# Revit family: QF_EVEREST_ESC59L
name_source: partatom
category: Specialty Equipment
revit_build: Autodesk Revit 2015 (Build: 20140606_1530(x64)
units: mm (PartAtom-declared; Revit-internal decimal feet)

## types (1)
- ESC59L
    Apparent Power = 173 VA
    Conn Conduit = Yes
    Conn Plug = NEMA 5-15P
    Cycle = 60 Hz
    Depth = 349 mm  [stored 1.14501 ft]
    Description = COUNTERTOP REFRIGERATED DISPLAY CASE
    Elec Conn Connection Height = 0 mm  [stored 0 ft]
    Elec Conn RI Height = 0 mm  [stored 0 ft]
    FL Amps = 2 A
    Foodservice Equipment Identifier = Yes
    HP = 1/8
    Height = 283 mm
    Identify Quantity as Lot = Yes
    Length = 1500 mm  [stored 4.92126 ft]
    Manufacturer = EVEREST
    Max Overcurrent Protection = 0 A
    Min Ckt Ampacity = 0 A
    Model = ESC59L
    Number of Poles = 1
    Phase = 1
    Volts = 115 V
    Watts = 173 W
    Weight in Pounds = 112

note: [stored X ft] marks values corroborated as IEEE doubles in the binary element streams (Revit-internal decimal feet)

## geometry (parser evidence)
native form markers: Sweep x2
no freeform markers — native parametric forms only
